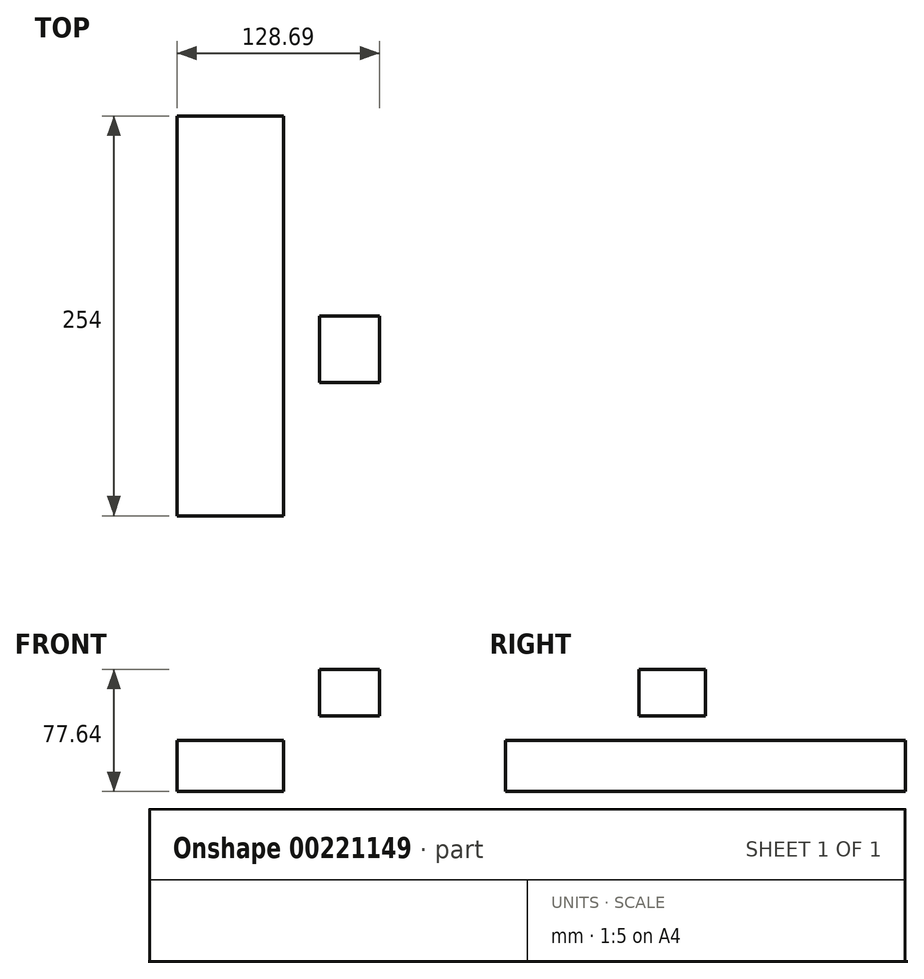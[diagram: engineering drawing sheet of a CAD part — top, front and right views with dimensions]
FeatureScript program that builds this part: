
annotation { "Feature Type Name" : "Feature", "Feature Type Description" : "" }
export const myFeature = defineFeature(function(context is Context, id is Id, definition is map)
    precondition{}
    {
        {
            var Q0;
            Q0=qCreatedBy(makeId("Front.planeOp"),FACE);
            var sketch = newSketch(context, id + "F0", { "sketchPlane" : qUnion([Q0])});
            skLineSegment(sketch, "E0.bottom", {"start": v(-34.44, 14.05) * mm, "end": v(33.23, 14.05) * mm});
            skLineSegment(sketch, "E0.top", {"start": v(-34.44, -18.58) * mm, "end": v(33.23, -18.58) * mm});
            skLineSegment(sketch, "E0.left", {"start": v(-34.44, 14.05) * mm, "end": v(-34.44, -18.58) * mm});
            skLineSegment(sketch, "E0.right", {"start": v(33.23, 14.05) * mm, "end": v(33.23, -18.58) * mm});
            skLineSegment(sketch, "E1.bottom", {"start": v(56.19, 59.06) * mm, "end": v(94.25, 59.06) * mm});
            skLineSegment(sketch, "E1.top", {"start": v(56.19, 29.45) * mm, "end": v(94.25, 29.45) * mm});
            skLineSegment(sketch, "E1.left", {"start": v(56.19, 59.06) * mm, "end": v(56.19, 29.45) * mm});
            skLineSegment(sketch, "E1.right", {"start": v(94.25, 59.06) * mm, "end": v(94.25, 29.45) * mm});
            skLineSegment(sketch, "E2", {"start": v(28.1, 14.05) * mm, "end": v(28.1, 29.15) * mm});
            skArc(sketch, "E3", {"start": v(28.1, 29.15) * mm, "mid": v(31.35, 37.02) * mm, "end": v(39.22, 40.28) * mm});
            skLineSegment(sketch, "E4", {"start": v(39.22, 40.28) * mm, "end": v(69.69, 40.28) * mm});
            skSolve(sketch);
        }
        {
            var Q0;
            {var subQ0=sQuery(id+"F0.wireOp",EDGE,"E1.bottom");Q0=makeQuery(id+"F0.imprint","IMPRINT",FACE,{"disambiguationData":[TD([[makeQuery(id+"F0.imprint","IMPRINT",EDGE,{"derivedFrom":subQ0}),-1.0]])]});}
            extrude(context, id + "F1", {"entities" : qUnion([Q0]), "depth" : 42.16 * mm});
        }
        {
            var Q0;
            Q0=makeQuery(id+"F0.imprint","IMPRINT",FACE,{"disambiguationData":[TD([[makeQuery(id+"F0.imprint","IMPRINT",EDGE,{"derivedFrom":sQuery(id+"F0.wireOp",EDGE,"E0.top")}),1.0]])]});
            extrude(context, id + "F2", {"entities" : qUnion([Q0]), "endBound" : BoundingType.SYMMETRIC, "depth" : 254 * mm});
        }
    });
